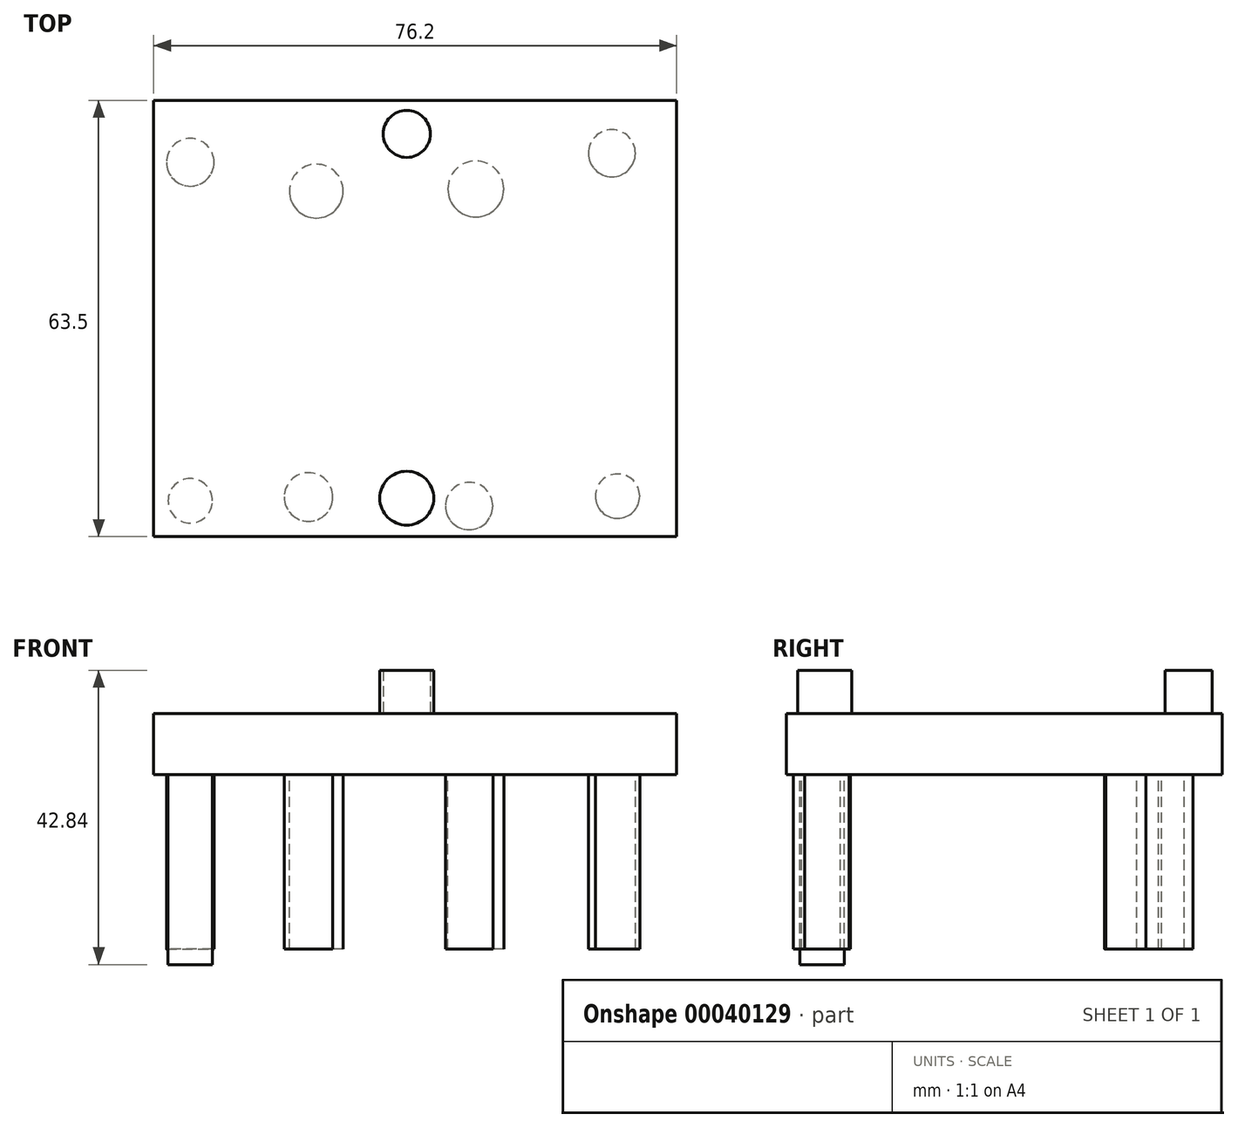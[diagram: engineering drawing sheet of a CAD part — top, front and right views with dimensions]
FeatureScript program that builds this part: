
annotation { "Feature Type Name" : "Feature", "Feature Type Description" : "" }
export const myFeature = defineFeature(function(context is Context, id is Id, definition is map)
    precondition{}
    {
        {
            var Q0;
            Q0=qCreatedBy(makeId("Top.planeOp"),FACE);
            var sketch = newSketch(context, id + "F0", { "sketchPlane" : qUnion([Q0])});
            skLineSegment(sketch, "E0.bottom", {"start": v(-52.5, 26.5) * mm, "end": v(23.7, 26.5) * mm});
            skLineSegment(sketch, "E0.top", {"start": v(-52.5, -37) * mm, "end": v(23.7, -37) * mm});
            skLineSegment(sketch, "E0.left", {"start": v(-52.5, 26.5) * mm, "end": v(-52.5, -37) * mm});
            skLineSegment(sketch, "E0.right", {"start": v(23.7, 26.5) * mm, "end": v(23.7, -37) * mm});
            skSolve(sketch);
        }
        {
            var Q0;
            Q0=makeQuery(id+"F0.imprint","IMPRINT",FACE,{"disambiguationData":[TD([[makeQuery(id+"F0.imprint","IMPRINT",EDGE,{"derivedFrom":sQuery(id+"F0.wireOp",EDGE,"E0.bottom")}),-1.0]])]});
            extrude(context, id + "F1", {"entities" : qUnion([Q0]), "depth" : 8.88 * mm});
        }
        {
            var Q0;
            Q0=makeQuery(id+"F1.opExtrude","CAP_FACE",FACE,{"disambiguationData":[OSD([sQuery(id+"F0.wireOp",EDGE,"E0.bottom"),sQuery(id+"F0.wireOp",EDGE,"E0.top"),sQuery(id+"F0.wireOp",EDGE,"E0.left"),sQuery(id+"F0.wireOp",EDGE,"E0.right")])],"isStart":true});
            var sketch = newSketch(context, id + "F2", { "sketchPlane" : qUnion([Q0])});
            skCircle(sketch, "E1", {"center": v(-47.16, 31.8) * mm, "radius": 3.23 * mm});
            skCircle(sketch, "E2", {"center": v(-47.16, -17.49) * mm, "radius": 3.47 * mm});
            skCircle(sketch, "E3", {"center": v(14.28, -18.8) * mm, "radius": 3.42 * mm});
            skCircle(sketch, "E4", {"center": v(15.1, 31.13) * mm, "radius": 3.23 * mm});
            skSolve(sketch);
        }
        {
            var Q0;
            Q0=makeQuery(id+"F2.imprint","IMPRINT",FACE,{"disambiguationData":[TD([[makeQuery(id+"F2.imprint","IMPRINT",EDGE,{"derivedFrom":sQuery(id+"F2.wireOp",EDGE,"E1")}),1.0]])]});
            extrude(context, id + "F3", {"entities" : qUnion([Q0]), "operationType" : NewBodyOperationType.ADD, "depth" : 27.65 * mm});
        }
        {
            var Q0;
            Q0 = qSketchRegion(id + "F2", true);
            extrude(context, id + "F4", {"entities" : qUnion([Q0]), "operationType" : NewBodyOperationType.ADD, "depth" : 25.4 * mm});
        }
        {
            var Q0;
            Q0=makeQuery(id+"F1.opExtrude","CAP_FACE",FACE,{"disambiguationData":[OSD([sQuery(id+"F0.wireOp",EDGE,"E0.bottom"),sQuery(id+"F0.wireOp",EDGE,"E0.top"),sQuery(id+"F0.wireOp",EDGE,"E0.left"),sQuery(id+"F0.wireOp",EDGE,"E0.right")])],"isStart":false});
            var sketch = newSketch(context, id + "F5", { "sketchPlane" : qUnion([Q0])});
            skCircle(sketch, "E5", {"center": v(-15.6, -31.43) * mm, "radius": 3.93 * mm});
            skCircle(sketch, "E6", {"center": v(-15.6, 21.62) * mm, "radius": 3.43 * mm});
            skSolve(sketch);
        }
        {
            var Q0;
            Q0 = qSketchRegion(id + "F5", true);
            extrude(context, id + "F6", {"entities" : qUnion([Q0]), "operationType" : NewBodyOperationType.ADD, "depth" : 6.32 * mm});
        }
        {
            var Q0;
            Q0=makeQuery(id+"F1.opExtrude","CAP_FACE",FACE,{"disambiguationData":[OSD([sQuery(id+"F0.wireOp",EDGE,"E0.bottom"),sQuery(id+"F0.wireOp",EDGE,"E0.top"),sQuery(id+"F0.wireOp",EDGE,"E0.left"),sQuery(id+"F0.wireOp",EDGE,"E0.right")])],"isStart":false});
            var sketch = newSketch(context, id + "F7", { "sketchPlane" : qUnion([Q0])});
            skLineSegment(sketch, "E7", {"start": v(-15.6, 21.62) * mm, "end": v(-15.6, -27.5) * mm});
            skSolve(sketch);
        }
        {
            var Q0;
            Q0=sQuery(id+"F7.wireOp",EDGE,"E7");
            extrude(context, id + "F8", {"bodyType" : ToolBodyType.SURFACE, "surfaceEntities" : qUnion([Q0]), "depth" : 6.54 * mm});
        }
        {
            var Q0;
            Q0=makeQuery(id+"F1.opExtrude","CAP_FACE",FACE,{"disambiguationData":[OSD([sQuery(id+"F0.wireOp",EDGE,"E0.bottom"),sQuery(id+"F0.wireOp",EDGE,"E0.top"),sQuery(id+"F0.wireOp",EDGE,"E0.left"),sQuery(id+"F0.wireOp",EDGE,"E0.right")])],"isStart":true});
            var sketch = newSketch(context, id + "F9", { "sketchPlane" : qUnion([Q0])});
            skCircle(sketch, "E8", {"center": v(-29.92, 31.25) * mm, "radius": 3.54 * mm});
            skCircle(sketch, "E9", {"center": v(-28.8, -13.29) * mm, "radius": 3.92 * mm});
            skCircle(sketch, "E10", {"center": v(-5.55, -13.6) * mm, "radius": 4.08 * mm});
            skCircle(sketch, "E11", {"center": v(-6.52, 32.57) * mm, "radius": 3.45 * mm});
            skSolve(sketch);
        }
        {
            var Q0;
            Q0=makeQuery(id+"F9.imprint","IMPRINT",FACE,{"disambiguationData":[TD([[makeQuery(id+"F9.imprint","IMPRINT",EDGE,{"derivedFrom":sQuery(id+"F9.wireOp",EDGE,"E10")}),1.0]])]});
            var Q1;
            Q1=makeQuery(id+"F9.imprint","IMPRINT",FACE,{"disambiguationData":[TD([[makeQuery(id+"F9.imprint","IMPRINT",EDGE,{"derivedFrom":sQuery(id+"F9.wireOp",EDGE,"E9")}),1.0]])]});
            var Q2;
            Q2=makeQuery(id+"F9.imprint","IMPRINT",FACE,{"disambiguationData":[TD([[makeQuery(id+"F9.imprint","IMPRINT",EDGE,{"derivedFrom":sQuery(id+"F9.wireOp",EDGE,"E8")}),1.0]])]});
            var Q3;
            Q3=makeQuery(id+"F9.imprint","IMPRINT",FACE,{"disambiguationData":[TD([[makeQuery(id+"F9.imprint","IMPRINT",EDGE,{"derivedFrom":sQuery(id+"F9.wireOp",EDGE,"E11")}),1.0]])]});
            extrude(context, id + "F10", {"entities" : qUnion([Q0, Q1, Q2, Q3]), "operationType" : NewBodyOperationType.ADD, "depth" : 25.4 * mm});
        }
    });
